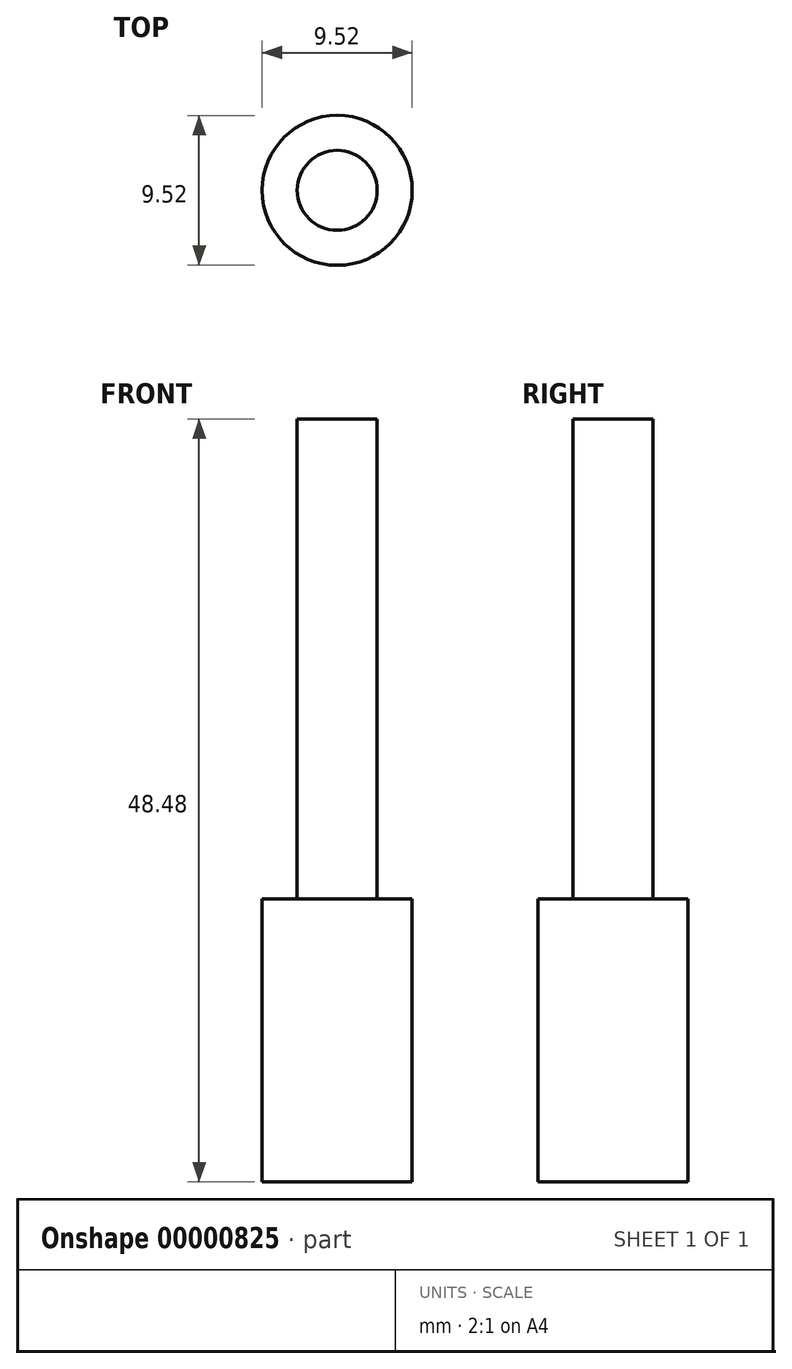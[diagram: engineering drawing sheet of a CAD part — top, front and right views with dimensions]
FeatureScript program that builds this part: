
annotation { "Feature Type Name" : "Feature", "Feature Type Description" : "" }
export const myFeature = defineFeature(function(context is Context, id is Id, definition is map)
    precondition{}
    {
        {
            var Q0;
            Q0=qCreatedBy(makeId("Top.planeOp"),FACE);
            var sketch = newSketch(context, id + "F0", { "sketchPlane" : qUnion([Q0])});
            skCircle(sketch, "E0", {"center": v(-8.26, 7.12) * mm, "radius": 4.76 * mm});
            skSolve(sketch);
        }
        {
            var Q0;
            Q0=makeQuery(id+"F0.imprint","IMPRINT",FACE,{"disambiguationData":[TD([[makeQuery(id+"F0.imprint","IMPRINT",EDGE,{"derivedFrom":sQuery(id+"F0.wireOp",EDGE,"E0")}),1.0]])]});
            extrude(context, id + "F1", {"entities" : qUnion([Q0]), "depth" : 18 * mm});
        }
        {
            var Q0;
            Q0=makeQuery(id+"F1.opExtrude","CAP_FACE",FACE,{"disambiguationData":[OSD([sQuery(id+"F0.wireOp",EDGE,"E0")])],"isStart":false});
            var sketch = newSketch(context, id + "F2", { "sketchPlane" : qUnion([Q0])});
            skCircle(sketch, "E1", {"center": v(-8.26, 7.12) * mm, "radius": 2.54 * mm});
            skSolve(sketch);
        }
        {
            var Q0;
            Q0 = qSketchRegion(id + "F2", true);
            extrude(context, id + "F3", {"entities" : qUnion([Q0]), "depth" : 30.48 * mm});
        }
    });
